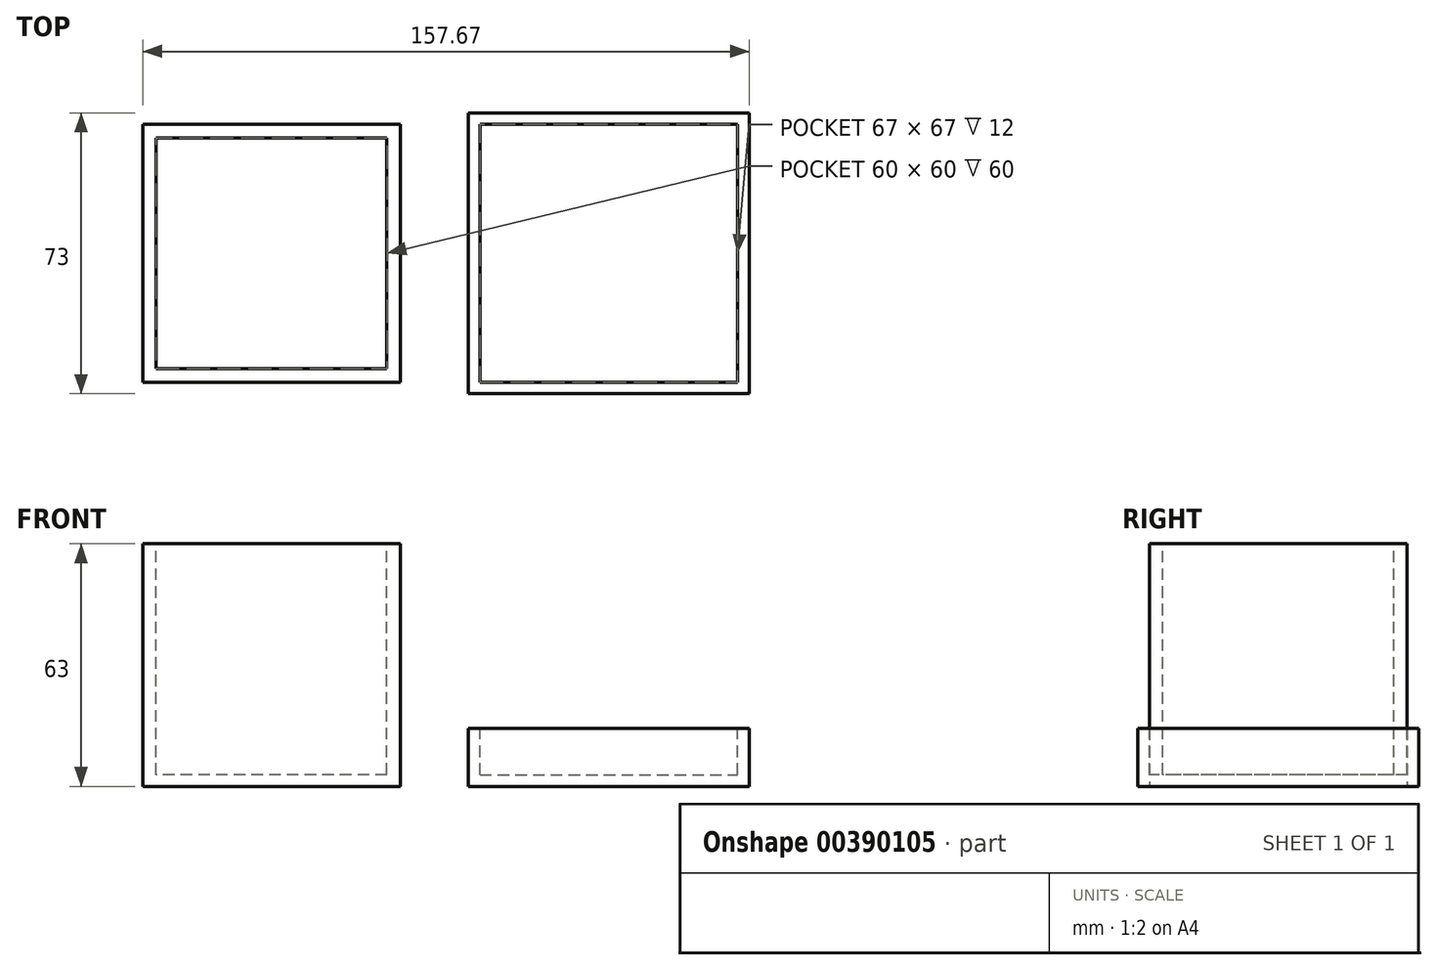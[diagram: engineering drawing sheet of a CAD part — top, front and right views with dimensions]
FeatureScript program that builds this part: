
annotation { "Feature Type Name" : "Feature", "Feature Type Description" : "" }
export const myFeature = defineFeature(function(context is Context, id is Id, definition is map)
    precondition{}
    {
        {
            var Q0;
            Q0=qCreatedBy(makeId("Top.planeOp"),FACE);
            var sketch = newSketch(context, id + "F0", { "sketchPlane" : qUnion([Q0])});
            skLineSegment(sketch, "E0.bottom", {"start": v(-33.5, 33.5) * mm, "end": v(33.5, 33.5) * mm});
            skLineSegment(sketch, "E0.top", {"start": v(-33.5, -33.5) * mm, "end": v(33.5, -33.5) * mm});
            skLineSegment(sketch, "E0.left", {"start": v(-33.5, 33.5) * mm, "end": v(-33.5, -33.5) * mm});
            skLineSegment(sketch, "E0.right", {"start": v(33.5, 33.5) * mm, "end": v(33.5, -33.5) * mm});
            skPoint(sketch, "E0.middle", {"position": v(0, 0) * mm});
            skSolve(sketch);
        }
        {
            var Q0;
            Q0=makeQuery(id+"F0.imprint","IMPRINT",FACE,{"disambiguationData":[TD([[makeQuery(id+"F0.imprint","IMPRINT",EDGE,{"derivedFrom":sQuery(id+"F0.wireOp",EDGE,"E0.bottom")}),-1.0]])]});
            extrude(context, id + "F1", {"entities" : qUnion([Q0]), "endBound" : BoundingType.SYMMETRIC, "depth" : 63 * mm});
        }
        {
            var Q0;
            Q0=makeQuery(id+"F1.opExtrude","CAP_FACE",FACE,{"disambiguationData":[OSD([sQuery(id+"F0.wireOp",EDGE,"E0.bottom"),sQuery(id+"F0.wireOp",EDGE,"E0.top"),sQuery(id+"F0.wireOp",EDGE,"E0.left"),sQuery(id+"F0.wireOp",EDGE,"E0.right")])],"isStart":false});
            var sketch = newSketch(context, id + "F2", { "sketchPlane" : qUnion([Q0])});
            skLineSegment(sketch, "E1.bottom", {"start": v(30, 30) * mm, "end": v(-30, 30) * mm});
            skLineSegment(sketch, "E1.top", {"start": v(30, -30) * mm, "end": v(-30, -30) * mm});
            skLineSegment(sketch, "E1.left", {"start": v(30, 30) * mm, "end": v(30, -30) * mm});
            skLineSegment(sketch, "E1.right", {"start": v(-30, 30) * mm, "end": v(-30, -30) * mm});
            skPoint(sketch, "E1.middle", {"position": v(0, 0) * mm});
            skSolve(sketch);
        }
        {
            var Q0;
            Q0 = qSketchRegion(id + "F2", true);
            extrude(context, id + "F3", {"entities" : qUnion([Q0]), "operationType" : NewBodyOperationType.REMOVE, "oppositeDirection" : true, "depth" : 60 * mm});
        }
        {
            var Q0;
            Q0=makeQuery(id+"F1.opExtrude","CAP_FACE",FACE,{"disambiguationData":[OSD([sQuery(id+"F0.wireOp",EDGE,"E0.bottom"),sQuery(id+"F0.wireOp",EDGE,"E0.top"),sQuery(id+"F0.wireOp",EDGE,"E0.left"),sQuery(id+"F0.wireOp",EDGE,"E0.right")])],"isStart":true});
            var sketch = newSketch(context, id + "F4", { "sketchPlane" : qUnion([Q0])});
            skPoint(sketch, "E2.middle", {"position": v(87.67, 0) * mm});
            skLineSegment(sketch, "E3.bottom", {"start": v(51.17, -36.5) * mm, "end": v(124.17, -36.5) * mm});
            skLineSegment(sketch, "E3.top", {"start": v(51.17, 36.5) * mm, "end": v(124.17, 36.5) * mm});
            skLineSegment(sketch, "E3.left", {"start": v(51.17, -36.5) * mm, "end": v(51.17, 36.5) * mm});
            skLineSegment(sketch, "E3.right", {"start": v(124.17, -36.5) * mm, "end": v(124.17, 36.5) * mm});
            skSolve(sketch);
        }
        {
            var Q0;
            Q0=makeQuery(id+"F4.imprint","IMPRINT",FACE,{"disambiguationData":[TD([[makeQuery(id+"F4.imprint","IMPRINT",EDGE,{"derivedFrom":sQuery(id+"F4.wireOp",EDGE,"E3.bottom")}),1.0]])]});
            extrude(context, id + "F5", {"entities" : qUnion([Q0]), "oppositeDirection" : true, "depth" : 15 * mm});
        }
        {
            var Q0;
            Q0=makeQuery(id+"F5.opExtrude","CAP_FACE",FACE,{"disambiguationData":[OSD([sQuery(id+"F4.wireOp",EDGE,"E3.bottom"),sQuery(id+"F4.wireOp",EDGE,"E3.top"),sQuery(id+"F4.wireOp",EDGE,"E3.left"),sQuery(id+"F4.wireOp",EDGE,"E3.right")])],"isStart":false});
            var sketch = newSketch(context, id + "F6", { "sketchPlane" : qUnion([Q0])});
            skLineSegment(sketch, "E4.0", {"start": v(51.17, 33.5) * mm, "end": v(124.17, 33.5) * mm});
            skLineSegment(sketch, "E5.0", {"start": v(121.17, 36.5) * mm, "end": v(121.17, -36.5) * mm});
            skLineSegment(sketch, "E6.0", {"start": v(51.17, -33.5) * mm, "end": v(124.17, -33.5) * mm});
            skLineSegment(sketch, "E7.0", {"start": v(54.17, 36.5) * mm, "end": v(54.17, -36.5) * mm});
            skSolve(sketch);
        }
        {
            var Q0;
            Q0 = qSketchRegion(id + "F6", true);
            extrude(context, id + "F7", {"entities" : qUnion([Q0]), "operationType" : NewBodyOperationType.REMOVE, "oppositeDirection" : true, "depth" : 12 * mm});
        }
    });
